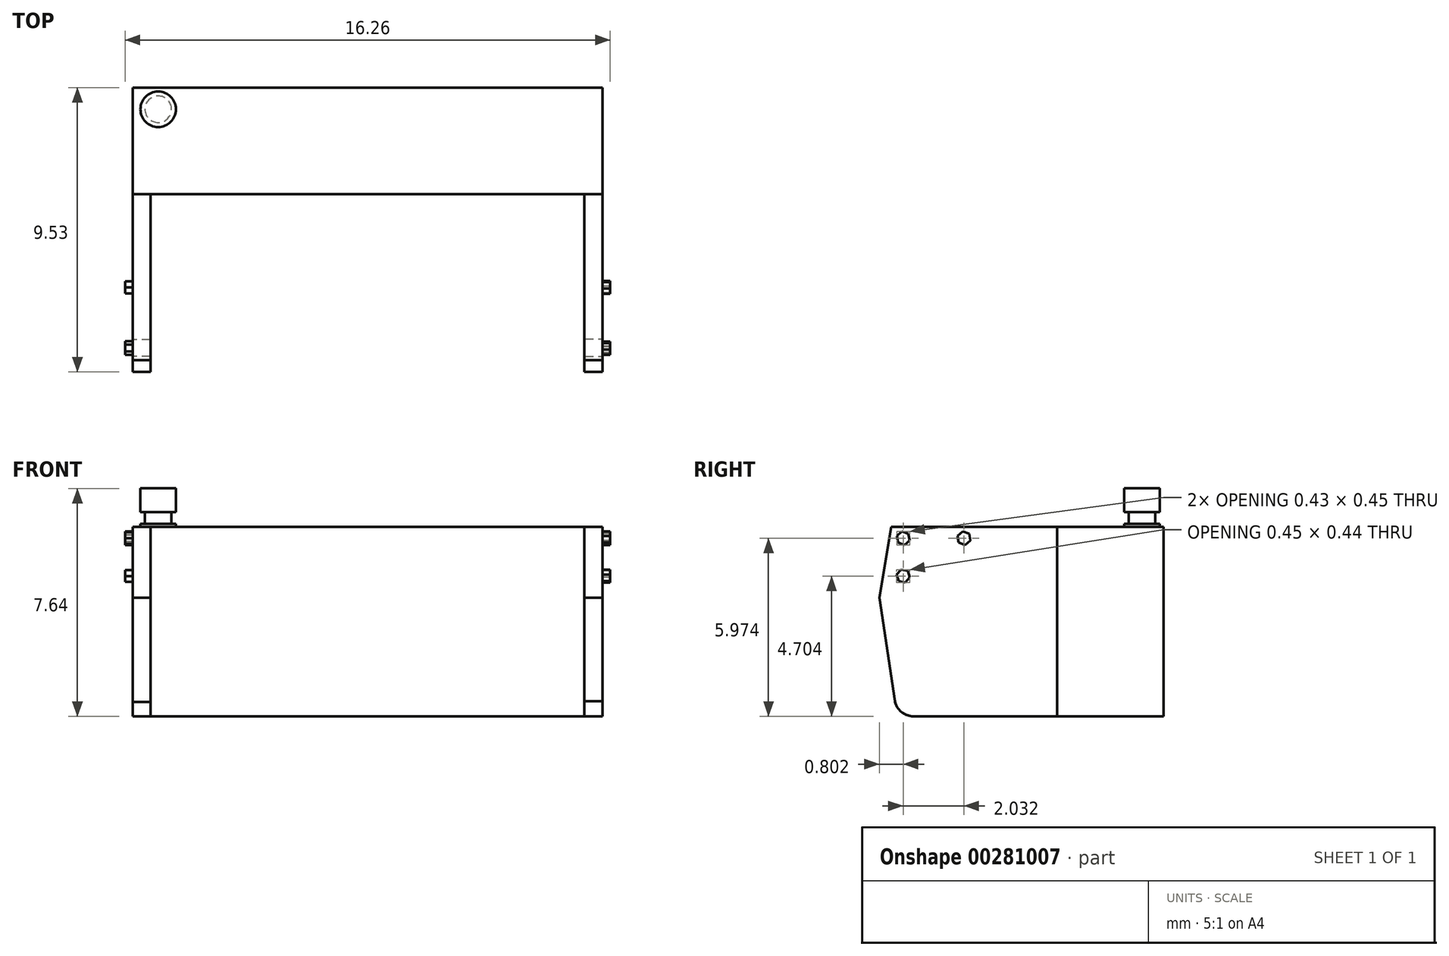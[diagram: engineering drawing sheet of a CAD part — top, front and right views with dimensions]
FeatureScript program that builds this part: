
annotation { "Feature Type Name" : "Feature", "Feature Type Description" : "" }
export const myFeature = defineFeature(function(context is Context, id is Id, definition is map)
    precondition{}
    {
        {
            var Q0;
            Q0=qCreatedBy(makeId("Front.planeOp"),FACE);
            var sketch = newSketch(context, id + "F0", { "sketchPlane" : qUnion([Q0])});
            skLineSegment(sketch, "E0.bottom", {"start": v(-7.87, 3.18) * mm, "end": v(7.87, 3.18) * mm});
            skLineSegment(sketch, "E0.top", {"start": v(-7.87, -3.18) * mm, "end": v(7.87, -3.18) * mm});
            skLineSegment(sketch, "E0.left", {"start": v(-7.87, 3.18) * mm, "end": v(-7.87, -3.18) * mm});
            skLineSegment(sketch, "E0.right", {"start": v(7.87, 3.18) * mm, "end": v(7.87, -3.18) * mm});
            skPoint(sketch, "E0.middle", {"position": v(0, 0) * mm});
            skSolve(sketch);
        }
        {
            var Q0;
            Q0=makeQuery(id+"F0.imprint","IMPRINT",FACE,{"disambiguationData":[TD([[makeQuery(id+"F0.imprint","IMPRINT",EDGE,{"derivedFrom":sQuery(id+"F0.wireOp",EDGE,"E0.bottom")}),-1.0]])]});
            extrude(context, id + "F1", {"entities" : qUnion([Q0]), "depth" : 3.57 * mm});
        }
        {
            var Q0;
            Q0=makeQuery(id+"F1.opExtrude","SWEPT_FACE",FACE,{"disambiguationData":[OSD([sQuery(id+"F0.wireOp",EDGE,"E0.left")])]});
            var sketch = newSketch(context, id + "F2", { "sketchPlane" : qUnion([Q0])});
            skLineSegment(sketch, "E1", {"start": v(3.57, 3.18) * mm, "end": v(9.53, 3.18) * mm});
            skLineSegment(sketch, "E2", {"start": v(3.57, -3.18) * mm, "end": v(8.44, -3.18) * mm});
            skLineSegment(sketch, "E3", {"start": v(9.13, 3.18) * mm, "end": v(9.53, 0.8) * mm});
            skLineSegment(sketch, "E4", {"start": v(9.53, 0.8) * mm, "end": v(9, -2.7) * mm});
            skPoint(sketch, "E5", {"position": v(8.33, -3.18) * mm});
            skPoint(sketch, "E6", {"position": v(9.02, -2.59) * mm});
            skArc(sketch, "E7", {"start": v(8.33, -3.18) * mm, "mid": v(8.8, -3.02) * mm, "end": v(9.02, -2.59) * mm});
            skPoint(sketch, "E8.orphan", {"position": v(8.93, -3.18) * mm});
            skPoint(sketch, "E9.orphan", {"position": v(9.53, -3.18) * mm});
            skSolve(sketch);
        }
        {
            var Q0;
            {var subQ0=sQuery(id+"F2.wireOp",EDGE,"E3");Q0=makeQuery(id+"F2.imprint","IMPRINT",FACE,{"disambiguationData":[TD([[makeQuery(id+"F2.imprint","IMPRINT",EDGE,{"derivedFrom":subQ0}),-1.0]])]});}
            extrude(context, id + "F3", {"entities" : qUnion([Q0]), "flatOperationType" : FlatOperationType.REMOVE, "oppositeDirection" : true, "offsetDistance" : 25.4 * mm, "depth" : 0.6 * mm, "domain" : OperationDomain.MODEL});
        }
        {
            var Q0;
            Q0=makeQuery(id+"F1.opExtrude","SWEPT_FACE",FACE,{"disambiguationData":[OSD([sQuery(id+"F0.wireOp",EDGE,"E0.right")])]});
            var sketch = newSketch(context, id + "F4", { "sketchPlane" : qUnion([Q0])});
            skLineSegment(sketch, "E10", {"start": v(-3.57, 3.18) * mm, "end": v(-9.53, 3.18) * mm});
            skLineSegment(sketch, "E11", {"start": v(-3.57, -3.18) * mm, "end": v(-8.42, -3.18) * mm});
            skLineSegment(sketch, "E12", {"start": v(-9.13, 3.18) * mm, "end": v(-9.52, 0.8) * mm});
            skLineSegment(sketch, "E13", {"start": v(-9.52, 0.8) * mm, "end": v(-9, -2.68) * mm});
            skPoint(sketch, "E14", {"position": v(-8.33, -3.18) * mm});
            skPoint(sketch, "E15", {"position": v(-9.02, -2.59) * mm});
            skArc(sketch, "E16", {"start": v(-9.02, -2.59) * mm, "mid": v(-8.8, -3.02) * mm, "end": v(-8.33, -3.18) * mm});
            skPoint(sketch, "E17.orphan", {"position": v(-8.93, -3.18) * mm});
            skPoint(sketch, "E18.orphan", {"position": v(-9.53, -3.18) * mm});
            skSolve(sketch);
        }
        {
            var Q0;
            {var subQ0=sQuery(id+"F4.wireOp",EDGE,"E12");Q0=makeQuery(id+"F4.imprint","IMPRINT",FACE,{"disambiguationData":[TD([[makeQuery(id+"F4.imprint","IMPRINT",EDGE,{"derivedFrom":subQ0}),1.0]])]});}
            extrude(context, id + "F5", {"entities" : qUnion([Q0]), "oppositeDirection" : true, "depth" : 0.6 * mm});
        }
        {
            var Q0;
            Q0=makeQuery(id+"F1.opExtrude","SWEPT_FACE",FACE,{"disambiguationData":[OSD([sQuery(id+"F0.wireOp",EDGE,"E0.bottom")])]});
            var sketch = newSketch(context, id + "F6", { "sketchPlane" : qUnion([Q0])});
            skCircle(sketch, "E19", {"center": v(-7.02, -0.72) * mm, "radius": 0.6 * mm});
            skSolve(sketch);
        }
        {
            var Q0;
            Q0=makeQuery(id+"F6.imprint","IMPRINT",FACE,{"disambiguationData":[TD([[makeQuery(id+"F6.imprint","IMPRINT",EDGE,{"derivedFrom":sQuery(id+"F6.wireOp",EDGE,"E19")}),1.0]])]});
            extrude(context, id + "F7", {"entities" : qUnion([Q0]), "operationType" : NewBodyOperationType.ADD, "depth" : 0.1 * mm});
        }
        {
            var Q0;
            Q0=makeQuery(id+"F7.opExtrude","CAP_FACE",FACE,{"disambiguationData":[OSD([sQuery(id+"F6.wireOp",EDGE,"E19")])],"isStart":false});
            var sketch = newSketch(context, id + "F8", { "sketchPlane" : qUnion([Q0])});
            skCircle(sketch, "E20", {"center": v(-7.02, -0.72) * mm, "radius": 0.44 * mm});
            skSolve(sketch);
        }
        {
            var Q0;
            Q0=makeQuery(id+"F8.imprint","IMPRINT",FACE,{"disambiguationData":[TD([[makeQuery(id+"F8.imprint","IMPRINT",EDGE,{"derivedFrom":sQuery(id+"F8.wireOp",EDGE,"E20")}),1.0]])]});
            extrude(context, id + "F9", {"entities" : qUnion([Q0]), "operationType" : NewBodyOperationType.ADD, "depth" : 0.4 * mm});
        }
        {
            var Q0;
            Q0=makeQuery(id+"F3.opExtrude","CAP_FACE",FACE,{"disambiguationData":[OSD([sQuery(id+"F0.wireOp",EDGE,"E0.left"),sQuery(id+"F2.wireOp",EDGE,"E1"),sQuery(id+"F2.wireOp",EDGE,"E2"),sQuery(id+"F2.wireOp",EDGE,"E3"),sQuery(id+"F2.wireOp",EDGE,"E4"),sQuery(id+"F2.wireOp",EDGE,"E7")])],"isStart":true});
            var sketch = newSketch(context, id + "F10", { "sketchPlane" : qUnion([Q0])});
            skCircle(sketch, "E21.cCircle", {"center": v(8.73, 2.8) * mm, "radius": 0.2 * mm, "construction": true});
            skLineSegment(sketch, "E21.0", {"start": v(8.84, 2.6) * mm, "end": v(8.61, 2.6) * mm});
            skLineSegment(sketch, "E21.1", {"start": v(8.61, 2.6) * mm, "end": v(8.5, 2.8) * mm});
            skLineSegment(sketch, "E21.2", {"start": v(8.5, 2.8) * mm, "end": v(8.61, 3) * mm});
            skLineSegment(sketch, "E21.3", {"start": v(8.61, 3) * mm, "end": v(8.84, 3) * mm});
            skLineSegment(sketch, "E21.4", {"start": v(8.84, 3) * mm, "end": v(8.96, 2.8) * mm});
            skLineSegment(sketch, "E21.5", {"start": v(8.96, 2.8) * mm, "end": v(8.84, 2.6) * mm});
            skPoint(sketch, "E21.0.midPoint", {"position": v(8.73, 2.6) * mm});
            skCircle(sketch, "E22.cCircle", {"center": v(6.7, 2.8) * mm, "radius": 0.2 * mm, "construction": true});
            skLineSegment(sketch, "E22.0", {"start": v(6.9, 2.69) * mm, "end": v(6.7, 2.56) * mm});
            skLineSegment(sketch, "E22.1", {"start": v(6.7, 2.56) * mm, "end": v(6.5, 2.67) * mm});
            skLineSegment(sketch, "E22.2", {"start": v(6.5, 2.67) * mm, "end": v(6.5, 2.9) * mm});
            skLineSegment(sketch, "E22.3", {"start": v(6.5, 2.9) * mm, "end": v(6.69, 3.02) * mm});
            skLineSegment(sketch, "E22.4", {"start": v(6.69, 3.02) * mm, "end": v(6.9, 2.91) * mm});
            skLineSegment(sketch, "E22.5", {"start": v(6.9, 2.91) * mm, "end": v(6.9, 2.69) * mm});
            skPoint(sketch, "E22.0.midPoint", {"position": v(6.8, 2.62) * mm});
            skCircle(sketch, "E23.cCircle", {"center": v(8.73, 1.52) * mm, "radius": 0.2 * mm, "construction": true});
            skPoint(sketch, "E23.cCircle.perimeterSnap0", {"position": v(8.9, 2.7) * mm});
            skLineSegment(sketch, "E23.0", {"start": v(8.96, 1.52) * mm, "end": v(8.84, 1.33) * mm});
            skLineSegment(sketch, "E23.1", {"start": v(8.84, 1.33) * mm, "end": v(8.61, 1.33) * mm});
            skLineSegment(sketch, "E23.2", {"start": v(8.61, 1.33) * mm, "end": v(8.5, 1.52) * mm});
            skLineSegment(sketch, "E23.3", {"start": v(8.5, 1.52) * mm, "end": v(8.61, 1.72) * mm});
            skLineSegment(sketch, "E23.4", {"start": v(8.61, 1.72) * mm, "end": v(8.84, 1.72) * mm});
            skLineSegment(sketch, "E23.5", {"start": v(8.84, 1.72) * mm, "end": v(8.96, 1.52) * mm});
            skPoint(sketch, "E23.0.midPoint", {"position": v(8.9, 1.42) * mm});
            skPoint(sketch, "E23.0.midPoint.positionSnap0", {"position": v(8.9, 2.7) * mm});
            skSolve(sketch);
        }
        {
            var Q0;
            Q0=makeQuery(id+"F10.imprint","IMPRINT",FACE,{"disambiguationData":[TD([[makeQuery(id+"F10.imprint","IMPRINT",EDGE,{"derivedFrom":sQuery(id+"F10.wireOp",EDGE,"E21.0")}),-1.0]])]});
            extrude(context, id + "F11", {"entities" : qUnion([Q0]), "operationType" : NewBodyOperationType.ADD, "depth" : 0.25 * mm});
        }
        {
            var Q0;
            Q0=makeQuery(id+"F10.imprint","IMPRINT",FACE,{"disambiguationData":[TD([[makeQuery(id+"F10.imprint","IMPRINT",EDGE,{"derivedFrom":sQuery(id+"F10.wireOp",EDGE,"E23.0")}),-1.0]])]});
            extrude(context, id + "F12", {"entities" : qUnion([Q0]), "operationType" : NewBodyOperationType.ADD, "depth" : 0.25 * mm});
        }
        {
            var Q0;
            Q0=makeQuery(id+"F10.imprint","IMPRINT",FACE,{"disambiguationData":[TD([[makeQuery(id+"F10.imprint","IMPRINT",EDGE,{"derivedFrom":sQuery(id+"F10.wireOp",EDGE,"E22.0")}),-1.0]])]});
            extrude(context, id + "F13", {"entities" : qUnion([Q0]), "operationType" : NewBodyOperationType.ADD, "depth" : 0.25 * mm});
        }
        {
            var Q0;
            Q0=makeQuery(id+"F5.opExtrude","CAP_FACE",FACE,{"disambiguationData":[OSD([sQuery(id+"F0.wireOp",EDGE,"E0.right"),sQuery(id+"F4.wireOp",EDGE,"E10"),sQuery(id+"F4.wireOp",EDGE,"E11"),sQuery(id+"F4.wireOp",EDGE,"E12"),sQuery(id+"F4.wireOp",EDGE,"E13"),sQuery(id+"F4.wireOp",EDGE,"E16")])],"isStart":true});
            var sketch = newSketch(context, id + "F14", { "sketchPlane" : qUnion([Q0])});
            skCircle(sketch, "E24.cCircle", {"center": v(-8.73, 2.8) * mm, "radius": 0.2 * mm, "construction": true});
            skLineSegment(sketch, "E24.0", {"start": v(-8.51, 2.72) * mm, "end": v(-8.69, 2.57) * mm});
            skLineSegment(sketch, "E24.1", {"start": v(-8.69, 2.57) * mm, "end": v(-8.9, 2.65) * mm});
            skLineSegment(sketch, "E24.2", {"start": v(-8.9, 2.65) * mm, "end": v(-8.94, 2.87) * mm});
            skLineSegment(sketch, "E24.3", {"start": v(-8.94, 2.87) * mm, "end": v(-8.77, 3.02) * mm});
            skLineSegment(sketch, "E24.4", {"start": v(-8.77, 3.02) * mm, "end": v(-8.55, 2.94) * mm});
            skLineSegment(sketch, "E24.5", {"start": v(-8.55, 2.94) * mm, "end": v(-8.51, 2.72) * mm});
            skPoint(sketch, "E24.0.midPoint", {"position": v(-8.6, 2.64) * mm});
            skCircle(sketch, "E25.cCircle", {"center": v(-6.7, 2.8) * mm, "radius": 0.2 * mm, "construction": true});
            skLineSegment(sketch, "E25.0", {"start": v(-6.48, 2.72) * mm, "end": v(-6.66, 2.57) * mm});
            skLineSegment(sketch, "E25.1", {"start": v(-6.66, 2.57) * mm, "end": v(-6.87, 2.65) * mm});
            skLineSegment(sketch, "E25.2", {"start": v(-6.87, 2.65) * mm, "end": v(-6.91, 2.87) * mm});
            skLineSegment(sketch, "E25.3", {"start": v(-6.91, 2.87) * mm, "end": v(-6.74, 3.02) * mm});
            skLineSegment(sketch, "E25.4", {"start": v(-6.74, 3.02) * mm, "end": v(-6.52, 2.94) * mm});
            skLineSegment(sketch, "E25.5", {"start": v(-6.52, 2.94) * mm, "end": v(-6.48, 2.72) * mm});
            skPoint(sketch, "E25.0.midPoint", {"position": v(-6.57, 2.64) * mm});
            skCircle(sketch, "E26.cCircle", {"center": v(-8.73, 1.52) * mm, "radius": 0.2 * mm, "construction": true});
            skLineSegment(sketch, "E26.0", {"start": v(-8.8, 1.74) * mm, "end": v(-8.58, 1.7) * mm});
            skLineSegment(sketch, "E26.1", {"start": v(-8.58, 1.7) * mm, "end": v(-8.5, 1.48) * mm});
            skLineSegment(sketch, "E26.2", {"start": v(-8.5, 1.48) * mm, "end": v(-8.66, 1.3) * mm});
            skLineSegment(sketch, "E26.3", {"start": v(-8.66, 1.3) * mm, "end": v(-8.88, 1.35) * mm});
            skLineSegment(sketch, "E26.4", {"start": v(-8.88, 1.35) * mm, "end": v(-8.95, 1.57) * mm});
            skLineSegment(sketch, "E26.5", {"start": v(-8.95, 1.57) * mm, "end": v(-8.8, 1.74) * mm});
            skPoint(sketch, "E26.0.midPoint", {"position": v(-8.69, 1.72) * mm});
            skSolve(sketch);
        }
        {
            var Q0;
            Q0=makeQuery(id+"F14.imprint","IMPRINT",FACE,{"disambiguationData":[TD([[makeQuery(id+"F14.imprint","IMPRINT",EDGE,{"derivedFrom":sQuery(id+"F14.wireOp",EDGE,"E24.0")}),-1.0]])]});
            extrude(context, id + "F15", {"entities" : qUnion([Q0]), "operationType" : NewBodyOperationType.ADD, "depth" : 0.25 * mm});
        }
        {
            var Q0;
            Q0=makeQuery(id+"F14.imprint","IMPRINT",FACE,{"disambiguationData":[TD([[makeQuery(id+"F14.imprint","IMPRINT",EDGE,{"derivedFrom":sQuery(id+"F14.wireOp",EDGE,"E25.0")}),-1.0]])]});
            extrude(context, id + "F16", {"entities" : qUnion([Q0]), "operationType" : NewBodyOperationType.ADD, "depth" : 0.25 * mm});
        }
        {
            var Q0;
            Q0=makeQuery(id+"F14.imprint","IMPRINT",FACE,{"disambiguationData":[TD([[makeQuery(id+"F14.imprint","IMPRINT",EDGE,{"derivedFrom":sQuery(id+"F14.wireOp",EDGE,"E26.0")}),-1.0]])]});
            extrude(context, id + "F17", {"entities" : qUnion([Q0]), "operationType" : NewBodyOperationType.ADD, "depth" : 0.25 * mm});
        }
        {
            var Q0;
            Q0=makeQuery(id+"F9.opExtrude","CAP_FACE",FACE,{"disambiguationData":[OSD([sQuery(id+"F8.wireOp",EDGE,"E20")])],"isStart":false});
            var sketch = newSketch(context, id + "F18", { "sketchPlane" : qUnion([Q0])});
            skCircle(sketch, "E27", {"center": v(-7.02, -0.72) * mm, "radius": 0.6 * mm});
            skSolve(sketch);
        }
        {
            var Q0;
            Q0=makeQuery(id+"F18.imprint","IMPRINT",FACE,{"disambiguationData":[TD([[makeQuery(id+"F18.imprint","IMPRINT",EDGE,{"derivedFrom":makeQuery(id+"F9.opExtrude","CAP_EDGE",EDGE,{"disambiguationData":[OSD([sQuery(id+"F8.wireOp",EDGE,"E20")])],"isStart":false})}),1.0]])]});
            var Q1;
            Q1=makeQuery(id+"F18.imprint","IMPRINT",FACE,{"disambiguationData":[TD([[makeQuery(id+"F18.imprint","IMPRINT",EDGE,{"derivedFrom":sQuery(id+"F18.wireOp",EDGE,"E27")}),1.0]])]});
            extrude(context, id + "F19", {"entities" : qUnion([Q0, Q1]), "operationType" : NewBodyOperationType.ADD, "depth" : 0.8 * mm});
        }
    });
